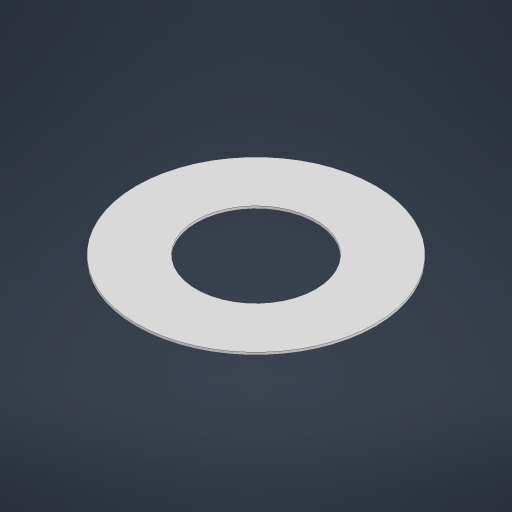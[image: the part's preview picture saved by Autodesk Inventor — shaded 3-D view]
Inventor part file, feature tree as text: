
AUTODESK INVENTOR PART (.ipt)
format: ipt  version: 2024.1 (Build 281209000, 209)  size: 409,600 bytes
history: native  units: mm
features: other x1, extrude x1, sketch x1
ambient origin geometry x8: Origin, YZ Plane, XZ Plane, XY Plane, X Axis, Y Axis, Z Axis, Center Point
bodies: Body1 (feature_tree)
feature tree (3):
  other  "솔리드1"
  extrude  "돌출1"  Depth=10.0mm
  sketch  "스케치1"
